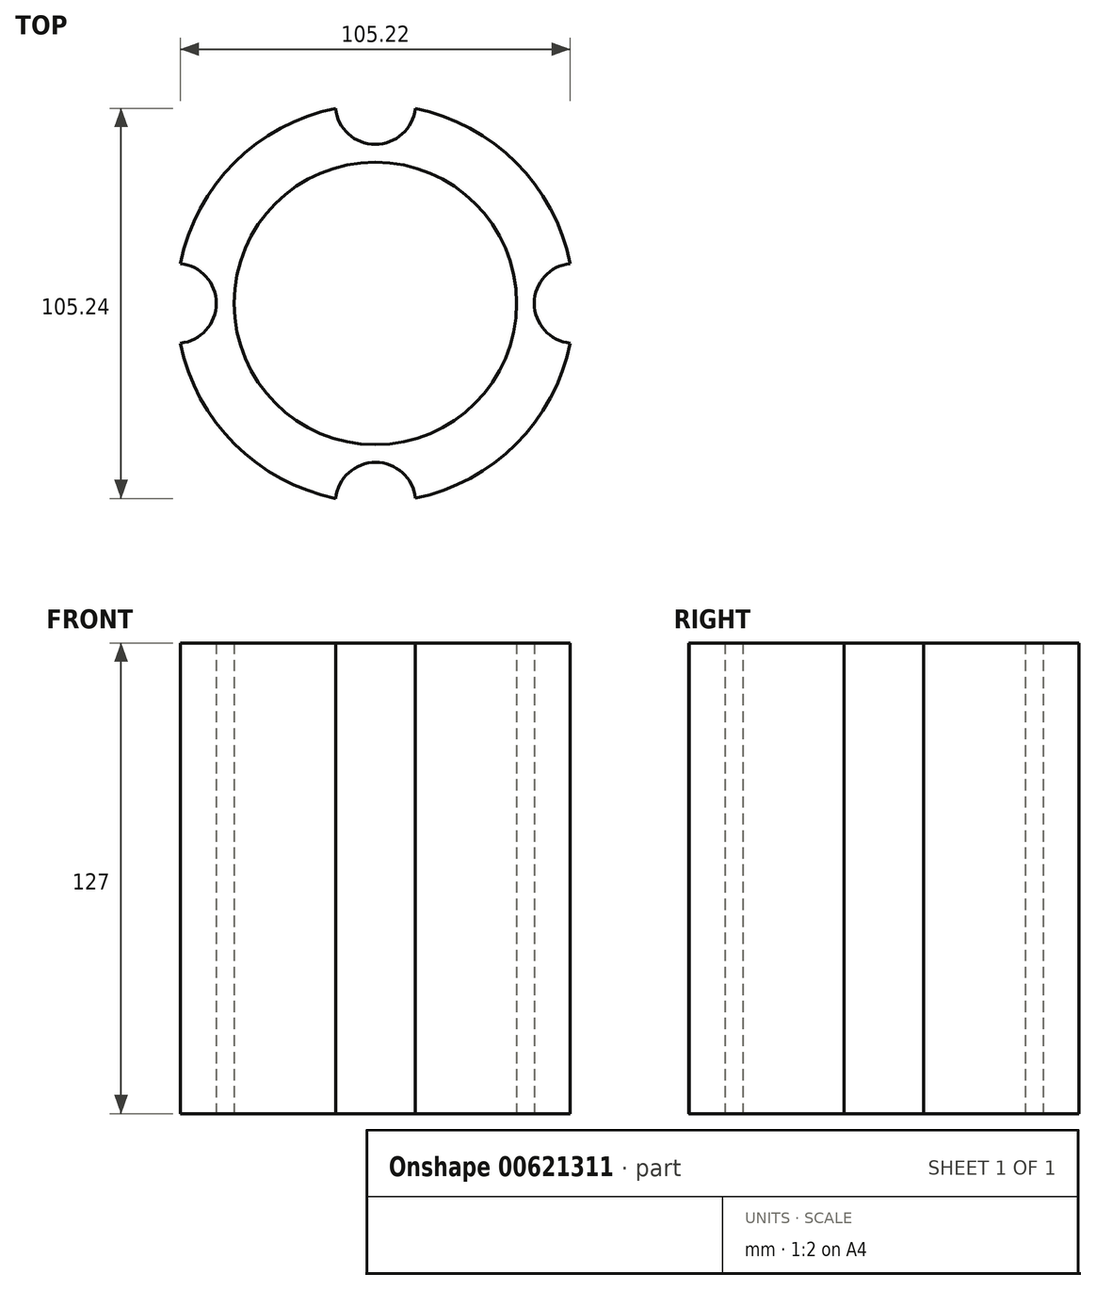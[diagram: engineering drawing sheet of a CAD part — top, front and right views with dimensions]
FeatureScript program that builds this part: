
annotation { "Feature Type Name" : "Feature", "Feature Type Description" : "" }
export const myFeature = defineFeature(function(context is Context, id is Id, definition is map)
    precondition{}
    {
        {
            var Q0;
            Q0=qCreatedBy(makeId("Top.planeOp"),FACE);
            var sketch = newSketch(context, id + "F0", { "sketchPlane" : qUnion([Q0])});
            skCircle(sketch, "E0", {"center": v(0, 0) * mm, "radius": 53.7 * mm});
            skCircle(sketch, "E1", {"center": v(127, 0) * mm, "radius": 53.7 * mm});
            skCircle(sketch, "E2", {"center": v(0, 0) * mm, "radius": 38.1 * mm});
            skCircle(sketch, "E3", {"center": v(0.08, -53.7) * mm, "radius": 10.8 * mm});
            skCircle(sketch, "E4", {"center": v(53.7, 0) * mm, "radius": 10.8 * mm});
            skCircle(sketch, "E5", {"center": v(0, 53.7) * mm, "radius": 10.8 * mm});
            skCircle(sketch, "E6", {"center": v(-53.7, 0) * mm, "radius": 10.8 * mm});
            skSolve(sketch);
        }
        {
            var Q0;
            Q0=makeQuery(id+"F0.imprint","IMPRINT",FACE,{"disambiguationData":[TD([[makeQuery(id+"F0.imprint","IMPRINT",EDGE,{"derivedFrom":sQuery(id+"F0.wireOp",EDGE,"E2")}),-1.0]])]});
            extrude(context, id + "F1", {"entities" : qUnion([Q0]), "depth" : 127 * mm, "offsetDistance" : 25.4 * mm});
        }
    });
